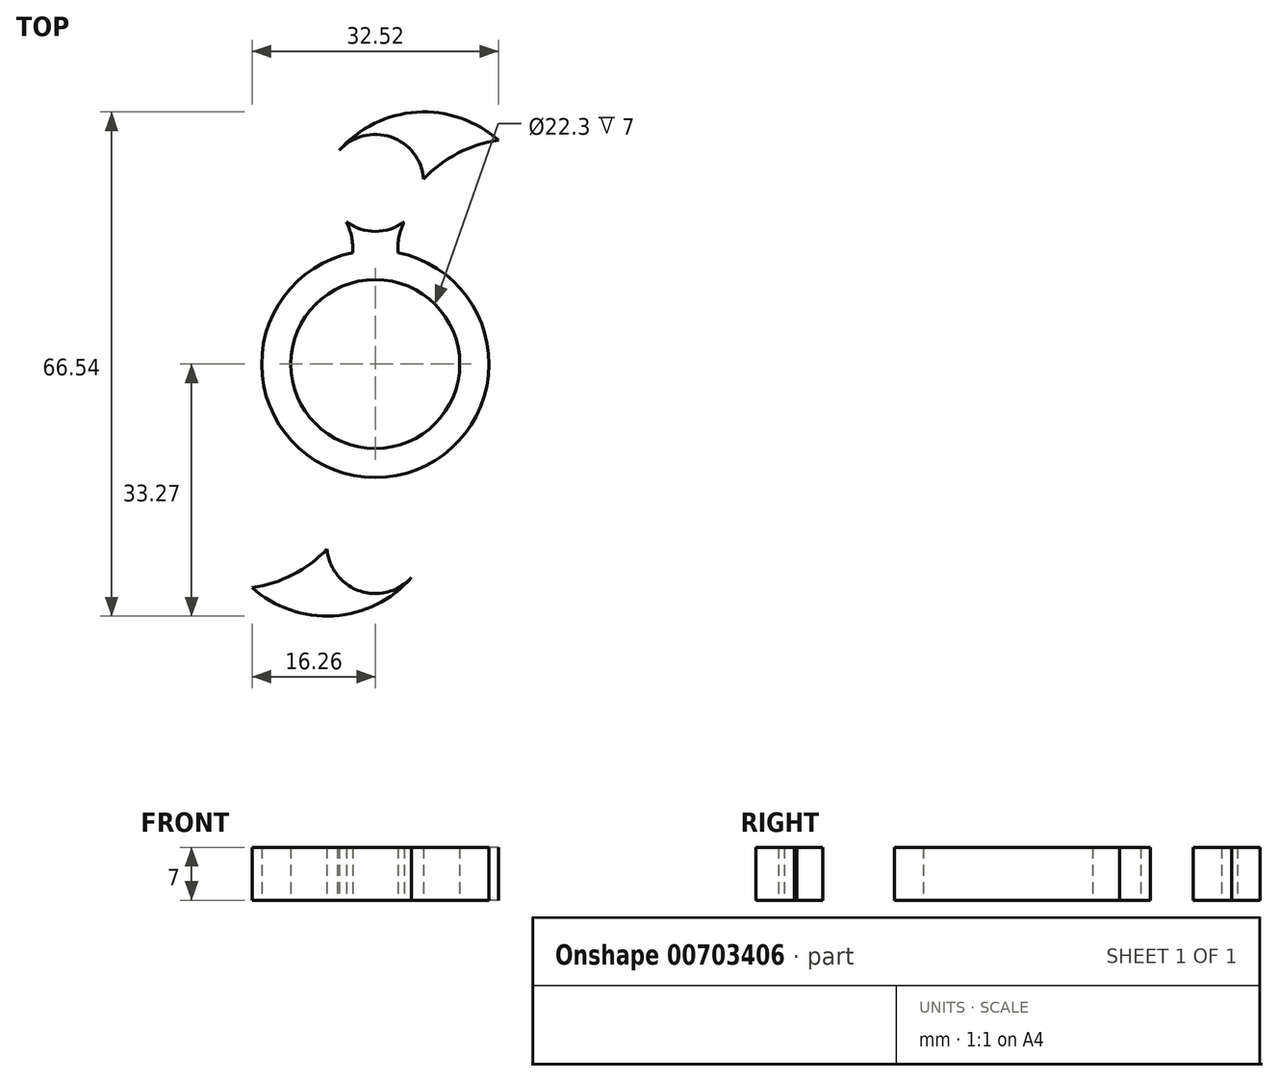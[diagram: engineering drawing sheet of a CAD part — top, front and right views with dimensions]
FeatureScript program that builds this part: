
annotation { "Feature Type Name" : "Feature", "Feature Type Description" : "" }
export const myFeature = defineFeature(function(context is Context, id is Id, definition is map)
    precondition{}
    {
        {
            var Q0;
            Q0=qCreatedBy(makeId("Top.planeOp"),FACE);
            var sketch = newSketch(context, id + "F0", { "sketchPlane" : qUnion([Q0])});
            skCircle(sketch, "E0", {"center": v(0, 0) * mm, "radius": 11.15 * mm});
            skCircle(sketch, "E1", {"center": v(0, 0) * mm, "radius": 15 * mm});
            skCircle(sketch, "E2", {"center": v(0, 23.9) * mm, "radius": 4.9 * mm});
            skCircle(sketch, "E3", {"center": v(0, 23.9) * mm, "radius": 6.4 * mm});
            skArc(sketch, "E4", {"start": v(16.26, 29.52) * mm, "mid": v(5.28, 33.23) * mm, "end": v(-5.01, 27.88) * mm});
            skArc(sketch, "E5", {"start": v(16.26, 29.52) * mm, "mid": v(8.9, 26.6) * mm, "end": v(3.66, 20.64) * mm});
            skCircle(sketch, "E6.MirrorC", {"center": v(0, -23.9) * mm, "radius": 4.9 * mm});
            skArc(sketch, "E7.MirrorC", {"start": v(-6.38, -24.42) * mm, "mid": v(5.95, -21.55) * mm, "end": v(-5.01, -27.88) * mm});
            skArc(sketch, "E8.MirrorCS", {"start": v(-4.74, -28.2) * mm, "mid": v(-4.88, -28.04) * mm, "end": v(-5.01, -27.88) * mm});
            skArc(sketch, "E9.MirrorCS", {"start": v(4.6, -22.2) * mm, "mid": v(4.1, -21.44) * mm, "end": v(3.66, -20.64) * mm});
            skArc(sketch, "E10.MirrorCS", {"start": v(-16.26, -29.52) * mm, "mid": v(-5.28, -33.23) * mm, "end": v(5.01, -27.88) * mm});
            skArc(sketch, "E11.MirrorC", {"start": v(3.66, -20.64) * mm, "mid": v(0, -28.8) * mm, "end": v(-3.66, -20.64) * mm});
            skCircle(sketch, "E12.MirrorC", {"center": v(0, -23.9) * mm, "radius": 6.4 * mm});
            skArc(sketch, "E13.MirrorCS", {"start": v(-16.26, -29.52) * mm, "mid": v(-8.9, -26.6) * mm, "end": v(-3.66, -20.64) * mm});
            skPoint(sketch, "E14.orphan", {"position": v(16.26, -29.52) * mm});
            skPoint(sketch, "E15.orphan", {"position": v(2.99, 14.7) * mm});
            skPoint(sketch, "E16.orphan", {"position": v(-2.99, 14.7) * mm});
            skPoint(sketch, "E17.MirrorCS.start.orphan", {"position": v(-2.99, -14.7) * mm});
            skPoint(sketch, "E18.MirrorCS.end.orphan", {"position": v(-3.66, -20.64) * mm});
            skPoint(sketch, "E19.orphan", {"position": v(2.99, -14.7) * mm});
            skPoint(sketch, "E20.end.orphan", {"position": v(-3.66, 20.64) * mm});
            skArc(sketch, "E21", {"start": v(-2.99, 14.7) * mm, "mid": v(-3.13, 16.79) * mm, "end": v(-3.82, 18.77) * mm});
            skArc(sketch, "E22.MirrorCS", {"start": v(2.99, 14.7) * mm, "mid": v(3.13, 16.79) * mm, "end": v(3.82, 18.77) * mm});
            skArc(sketch, "E23.MirrorCS", {"start": v(-2.99, -14.7) * mm, "mid": v(-3.13, -16.79) * mm, "end": v(-3.82, -18.77) * mm});
            skArc(sketch, "E24.MirrorCS", {"start": v(2.99, -14.7) * mm, "mid": v(3.13, -16.79) * mm, "end": v(3.82, -18.77) * mm});
            skSolve(sketch);
        }
        {
            var Q0;
            Q0=makeQuery(id+"F0.imprint","IMPRINT",FACE,{"disambiguationData":[TD([[makeQuery(id+"F0.imprint","IMPRINT",EDGE,{"derivedFrom":sQuery(id+"F0.wireOp",EDGE,"E0")}),-1.0]])]});
            var Q1;
            {var subQ0=sQuery(id+"F0.wireOp",EDGE,"E21");Q1=makeQuery(id+"F0.imprint","IMPRINT",FACE,{"disambiguationData":[TD([[makeQuery(id+"F0.imprint","IMPRINT",EDGE,{"derivedFrom":subQ0}),-1.0]])]});}
            var Q2;
            {var subQ4=sQuery(id+"F0.wireOp",EDGE,"E5");var subQ7=sQuery(id+"F0.wireOp",EDGE,"E2");var subQ8=makeQuery(id+"F0.imprint","INTERSECT",VERTEX,{"disambiguationData":[OD(0.0)],"derivedFrom":[subQ7,subQ4]});Q2=makeQuery(id+"F0.imprint","IMPRINT",FACE,{"disambiguationData":[TD([[makeQuery(id+"F0.imprint","IMPRINT",EDGE,{"disambiguationData":[TD([[subQ8,1.0]])],"derivedFrom":subQ7}),1.0]])]});}
            var Q3;
            {var subQ0=sQuery(id+"F0.wireOp",EDGE,"E5");var subQ1=sQuery(id+"F0.wireOp",EDGE,"E3");var subQ2=makeQuery(id+"F0.imprint","INTERSECT",VERTEX,{"derivedFrom":[subQ1,subQ0]});Q3=makeQuery(id+"F0.imprint","IMPRINT",FACE,{"disambiguationData":[TD([[makeQuery(id+"F0.imprint","IMPRINT",EDGE,{"disambiguationData":[TD([[subQ2,-1.0]])],"derivedFrom":subQ1}),-1.0]])]});}
            var Q4;
            {var subQ0=sQuery(id+"F0.wireOp",EDGE,"E23.MirrorCS");Q4=makeQuery(id+"F0.imprint","IMPRINT",FACE,{"disambiguationData":[TD([[makeQuery(id+"F0.imprint","IMPRINT",EDGE,{"derivedFrom":subQ0}),1.0]])]});}
            var Q5;
            {var subQ4=sQuery(id+"F0.wireOp",EDGE,"E8.MirrorCS");Q5=makeQuery(id+"F0.imprint","IMPRINT",FACE,{"disambiguationData":[TD([[makeQuery(id+"F0.imprint","IMPRINT",EDGE,{"derivedFrom":subQ4}),-1.0]])]});}
            var Q6;
            {var subQ3=sQuery(id+"F0.wireOp",EDGE,"E10.MirrorCS");var subQ6=sQuery(id+"F0.wireOp",EDGE,"E13.MirrorCS");var subQ8=makeQuery(id+"F0.imprint","INTERSECT",VERTEX,{"derivedFrom":[subQ3,subQ6]});Q6=makeQuery(id+"F0.imprint","IMPRINT",FACE,{"disambiguationData":[TD([[makeQuery(id+"F0.imprint","IMPRINT",EDGE,{"disambiguationData":[TD([[subQ8,-1.0]])],"derivedFrom":subQ3}),1.0]])]});}
            extrude(context, id + "F1", {"entities" : qUnion([Q0, Q1, Q2, Q3, Q4, Q5, Q6]), "depth" : 7 * mm, "offsetDistance" : 25 * mm});
        }
    });
